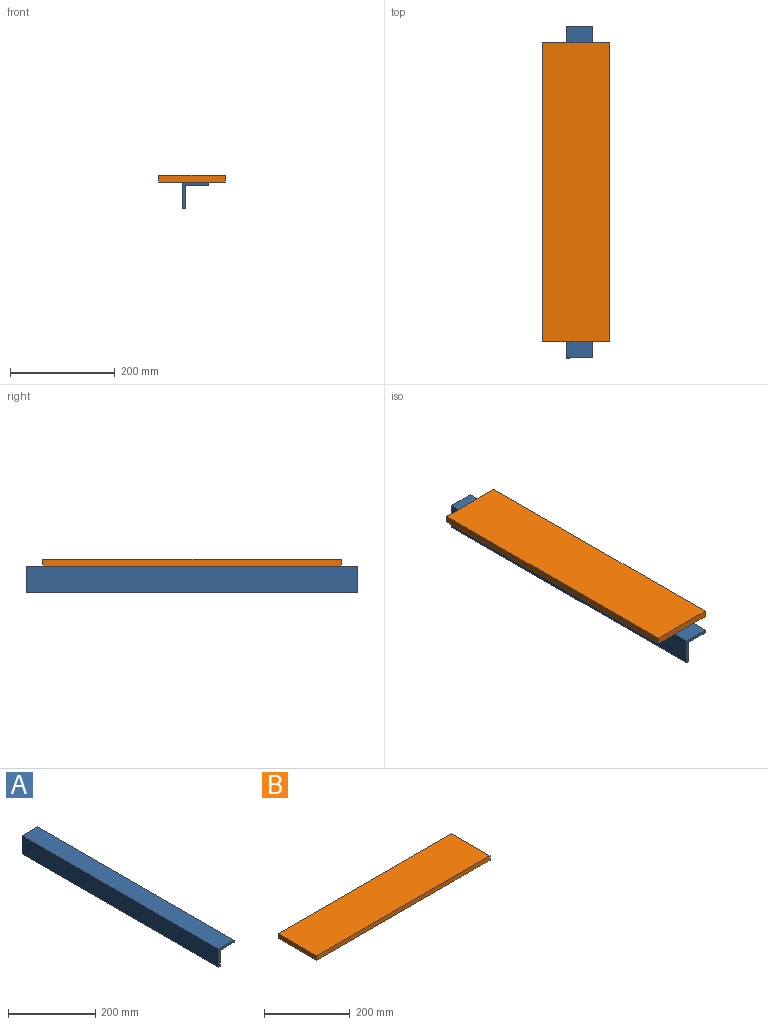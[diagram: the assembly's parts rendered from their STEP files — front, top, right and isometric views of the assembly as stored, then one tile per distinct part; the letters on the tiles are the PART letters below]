
ASSEMBLY  parts=2 mates=1
PART A: 8 faces, bbox 50.8x635x50.8 mm
  f0: plane 635x6.35mm, normal (0,0,-1), area 4032.3mm2, adj f1,f5,f6,f7
  f1: plane 635x44.45mm, normal (1,0,0), area 28225.8mm2, adj f0,f2,f6,f7
  f2: plane 635x44.45mm, normal (0,0,-1), area 28225.8mm2, adj f1,f3,f6,f7
  f3: plane 635x6.35mm, normal (1,0,0), area 4032.2mm2, adj f2,f4,f6,f7
  f4: plane 635x50.8mm, normal (0,0,1), area 32258mm2, adj f3,f5,f6,f7
  f5: plane 635x50.8mm, normal (-1,0,0), area 32258mm2, adj f0,f4,f6,f7
  f6: plane 50.8x50.8mm, normal (0,1,0), area 604.8mm2, adj f0,f1,f2,f3,f4,f5
  f7: plane 50.8x50.8mm, normal (0,-1,0), area 604.8mm2, adj f0,f1,f2,f3,f4,f5
PART B: 6 faces, bbox 571.5x127x12.7 mm
  f0: plane 127x12.7mm, normal (-1,0,0), area 1612.9mm2, adj f1,f3,f4,f5
  f1: plane 571.5x12.7mm, normal (0,-1,0), area 7258mm2, adj f0,f2,f4,f5
  f2: plane 127x12.7mm, normal (1,0,0), area 1612.9mm2, adj f1,f3,f4,f5
  f3: plane 571.5x12.7mm, normal (0,1,0), area 7258mm2, adj f0,f2,f4,f5
  f4: plane 571.5x127mm, normal (0,0,1), area 72580.5mm2, adj f0,f1,f2,f3
  f5: plane 571.5x127mm, normal (0,0,-1), area 72580.5mm2, adj f0,f1,f2,f3
PLACE A t=(1.04,-318.33,-25.51)mm fixed
PLACE B rot(axis=(-0.71,0.71,0),180deg) t=(-7.66,-0.83,37.99)mm
MATE fastened B.f4 <-> A.f4  axis (0,0,-1) through (-7.66,-0.83,25.29)mm
